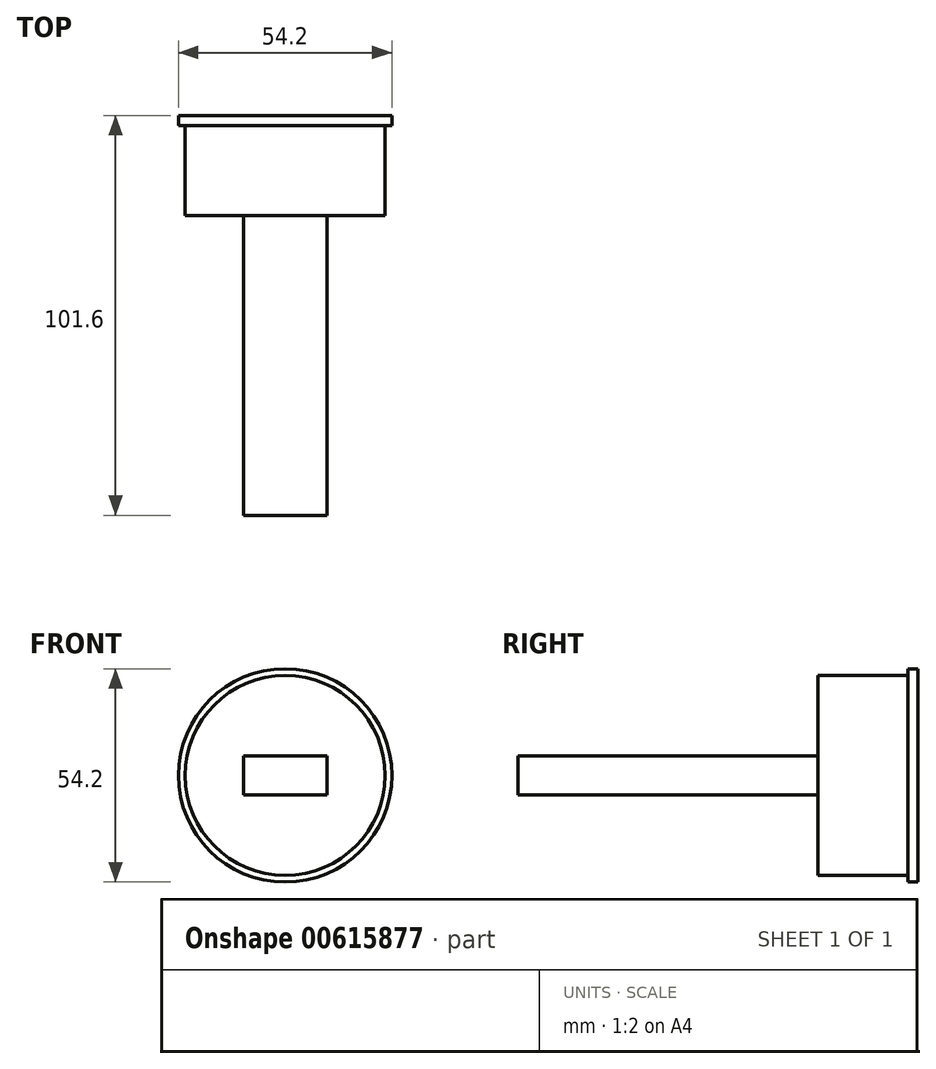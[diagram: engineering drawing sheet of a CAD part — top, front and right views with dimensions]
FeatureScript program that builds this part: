
annotation { "Feature Type Name" : "Feature", "Feature Type Description" : "" }
export const myFeature = defineFeature(function(context is Context, id is Id, definition is map)
    precondition{}
    {
        {
            var Q0;
            Q0=qCreatedBy(makeId("Front.planeOp"),FACE);
            var sketch = newSketch(context, id + "F0", { "sketchPlane" : qUnion([Q0])});
            skCircle(sketch, "E0", {"center": v(0, 0) * mm, "radius": 25.4 * mm});
            skSolve(sketch);
        }
        {
            var Q0;
            Q0 = qSketchRegion(id + "F0", true);
            extrude(context, id + "F1", {"entities" : qUnion([Q0]), "depth" : 25.4 * mm, "offsetDistance" : 25.4 * mm});
        }
        {
            var Q0;
            Q0=qCreatedBy(makeId("Front.planeOp"),FACE);
            var sketch = newSketch(context, id + "F2", { "sketchPlane" : qUnion([Q0])});
            skLineSegment(sketch, "E1.bottom", {"start": v(-10.58, 5) * mm, "end": v(10.58, 5) * mm});
            skLineSegment(sketch, "E1.top", {"start": v(-10.58, -5) * mm, "end": v(10.58, -5) * mm});
            skLineSegment(sketch, "E1.left", {"start": v(-10.58, 5) * mm, "end": v(-10.58, -5) * mm});
            skLineSegment(sketch, "E1.right", {"start": v(10.58, 5) * mm, "end": v(10.58, -5) * mm});
            skPoint(sketch, "E1.middle", {"position": v(0, 0) * mm});
            skSolve(sketch);
        }
        {
            var Q0;
            Q0 = qSketchRegion(id + "F2", true);
            extrude(context, id + "F3", {"entities" : qUnion([Q0]), "operationType" : NewBodyOperationType.ADD, "depth" : 101.6 * mm, "offsetDistance" : 25.4 * mm});
        }
        {
            var Q0;
            Q0=qCreatedBy(makeId("Front.planeOp"),FACE);
            var sketch = newSketch(context, id + "F4", { "sketchPlane" : qUnion([Q0])});
            skCircle(sketch, "E2", {"center": v(0, 0) * mm, "radius": 27.1 * mm});
            skSolve(sketch);
        }
        {
            var Q0;
            Q0 = qSketchRegion(id + "F4", true);
            extrude(context, id + "F5", {"entities" : qUnion([Q0]), "operationType" : NewBodyOperationType.ADD, "depth" : 2.54 * mm, "offsetDistance" : 25.4 * mm});
        }
    });
